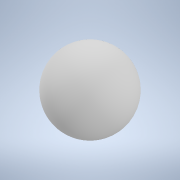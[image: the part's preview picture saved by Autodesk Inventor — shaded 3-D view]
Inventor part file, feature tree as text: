
AUTODESK INVENTOR PART (.ipt)
format: ipt  version: 2021 (Build 250183000, 183)  size: 115,712 bytes
history: native  units: in
note: dims shown in document units (in); Inventor stores cm internally (conversion verified against a paired STEP export)
features: revolve x1, sketch x1
ambient origin geometry x8: Origin, YZ Plane, XZ Plane, XY Plane, X Axis, Y Axis, Z Axis, Center Point
bodies: Solid1 (feature_tree)
feature tree (2):
  revolve  "Revolution1"  Angle=90.0deg
  sketch  "Sketch3"  dims[d1=11.811in d2=90.0deg]
